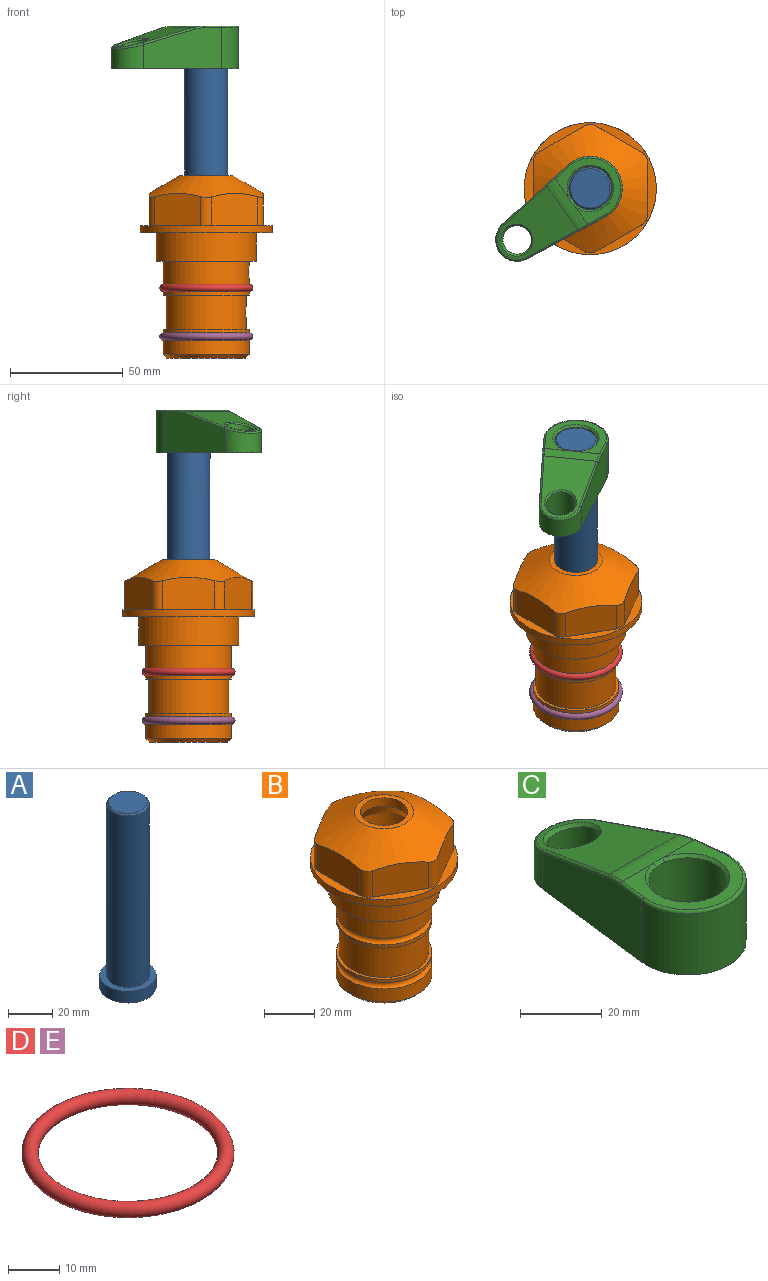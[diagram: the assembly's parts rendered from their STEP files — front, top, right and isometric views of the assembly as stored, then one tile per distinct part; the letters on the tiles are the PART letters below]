
ASSEMBLY  parts=5 mates=4
PART A: 6 faces, bbox 25.4x25.4x101.6 mm
  f0: plane 17.46x17.46mm, normal (0,0,1), area 239.5mm2, adj f5
  f1: plane 25.4x25.4mm, normal (0,0,-1), area 506.7mm2, adj f2
  f2: cylinder r=12.7mm len=25.4mm, axis (0,0,1), area 506.7mm2, adj f1,f3
  f3: plane 25.4x25.4mm, normal (0,0,1), area 221.7mm2, adj f2,f4
  f4: cylinder r=9.53mm len=94.46mm, axis (0,0,1), area 5653mm2, adj f3,f5
  f5: cone r=8.73mm half-angle=45deg, axis (0,0,-1), area 64.4mm2, adj f0,f4
PART B: 36 faces, bbox 58.7x58.7x81 mm
  f0: cylinder r=17.78mm len=35.56mm, axis (0,0,1), area 1670.8mm2, adj f23,f24,f31
  f1: cylinder r=19.05mm len=38.1mm, axis (0,0,1), area 1191.9mm2, adj f26,f27,f30
  f2: plane 58.66x58.66mm, normal (0,0,-1), area 1150.6mm2, adj f3,f28
  f3: cylinder r=29.33mm len=58.66mm, axis (0,0,-1), area 585.1mm2, adj f2,f4
  f4: plane 58.66x58.66mm, normal (0,0,1), area 475.9mm2, adj f3,f5,f6,f7,f8,f9,f10,f11
  f5: plane 20.32x14.34mm, normal (-0.5,0.87,0), area 324.4mm2, adj f4,f15,f16,f17
  f6: plane 20.32x14.34mm, normal (0.5,0.87,0), area 324.4mm2, adj f4,f14,f15,f17
  f7: plane 23.48x14.34mm, normal (1,0,0), area 324.4mm2, adj f4,f13,f14,f17
  f8: plane 20.32x14.34mm, normal (0.5,-0.87,0), area 324.4mm2, adj f4,f12,f13,f17
  f9: plane 20.32x14.34mm, normal (-0.5,-0.87,0), area 324.4mm2, adj f4,f11,f12,f17
  f10: plane 23.48x14.34mm, normal (-1,0,0), area 324.4mm2, adj f4,f11,f16,f17
  f11: cylinder r=5.08mm len=12.85mm, axis (0,0,-1), area 67.2mm2, adj f4,f9,f10,f17
  f12: cylinder r=5.08mm len=12.85mm, axis (0,0,-1), area 67.2mm2, adj f4,f8,f9,f17
  f13: cylinder r=5.08mm len=12.85mm, axis (0,0,-1), area 67.2mm2, adj f4,f7,f8,f17
  f14: cylinder r=5.08mm len=12.85mm, axis (0,0,-1), area 67.2mm2, adj f4,f6,f7,f17
  f15: cylinder r=5.08mm len=12.85mm, axis (0,0,-1), area 67.2mm2, adj f4,f5,f6,f17
  f16: cylinder r=5.08mm len=12.85mm, axis (0,0,-1), area 67.2mm2, adj f4,f5,f10,f17
  f17: cone r=11.73mm half-angle=60deg, axis (0,0,-1), area 2071.8mm2, adj f5,f6,f7,f8,f9,f10,f11,f12
  f18: plane 23.46x23.46mm, normal (0,0,1), area 147.4mm2, adj f17,f35
  f19: plane 34.93x34.93mm, normal (0,0,-1), area 958mm2, adj f29
  f20: cylinder r=19.05mm len=38.1mm, axis (0,0,1), area 760.1mm2, adj f21,f29
  f21: torus R=19.05mm, axis (0,0,1), area 565.3mm2, adj f20,f22
  f22: cylinder r=19.05mm len=38.1mm, axis (0,0,1), area 190mm2, adj f21,f23
  f23: plane 38.1x38.1mm, normal (0,0,1), area 146.9mm2, adj f0,f22
  f24: plane 38.1x38.1mm, normal (0,0,-1), area 146.9mm2, adj f0,f25
  f25: cylinder r=19.05mm len=38.1mm, axis (0,0,1), area 190mm2, adj f24,f26
  f26: torus R=19.05mm, axis (0,0,1), area 565.3mm2, adj f1,f25
  f27: plane 44.45x44.45mm, normal (0,0,-1), area 411.7mm2, adj f1,f28
  f28: cylinder r=22.23mm len=44.45mm, axis (0,0,1), area 1773.5mm2, adj f2,f27
  f29: cone r=19.05mm half-angle=45deg, axis (0,0,1), area 257.5mm2, adj f19,f20
  f30: cylinder r=3.17mm len=6.75mm, axis (-1,0,0), area 128mm2, adj f1,f33
  f31: cylinder r=3.17mm len=6.35mm, axis (-1,0,0), area 102.5mm2, adj f0,f33
  f32: plane 25.4x25.4mm, normal (0,0,1), area 506.7mm2, adj f33
  f33: cylinder r=12.7mm len=66.42mm, axis (0,0,-1), area 5236.2mm2, adj f30,f31,f32,f34
  f34: cone r=9.53mm half-angle=30deg, axis (0,0,-1), area 443.4mm2, adj f33,f35
  f35: cylinder r=9.53mm len=19.05mm, axis (0,0,-1), area 240.9mm2, adj f18,f34
PART C: 31 faces, bbox 31.7x65.5x19.8 mm
  f0: plane 39.12x18.26mm, normal (0.99,0.12,0), area 612.2mm2, adj f1,f4,f7,f11,f13,f15
  f1: cylinder r=9.53mm len=18.91mm, axis (0,0,-1), area 296.1mm2, adj f0,f2,f7,f17
  f2: plane 39.12x18.26mm, normal (-0.99,0.12,0), area 612.2mm2, adj f1,f4,f7,f12,f14,f16
  f3: cylinder r=6.35mm len=12.7mm, axis (0,0,-1), area 362.4mm2, adj f7,f18
  f4: cylinder r=14.29mm len=28.58mm, axis (0,0,-1), area 882.2mm2, adj f0,f2,f7,f10
  f5: cylinder r=9.53mm len=19.05mm, axis (0,0,-1), area 1092.6mm2, adj f7,f19,f20
  f6: plane 26.99x23.69mm, normal (0,0,1), area 216.2mm2, adj f9,f10,f11,f12,f19
  f7: plane 63.5x28.58mm, normal (0,0,-1), area 661.8mm2, adj f0,f1,f2,f3,f4,f5,f22,f23
  f8: plane 33.52x23.6mm, normal (0,0.26,0.97), area 486mm2, adj f9,f15,f16,f17,f18
  f9: cylinder r=19.05mm len=24.72mm, axis (1,0,0), area 120.4mm2, adj f6,f8,f13,f14,f20
  f10: torus R=13.49mm, axis (0,0,1), area 59mm2, adj f4,f6,f11,f12
  f11: cylinder r=0.79mm len=8.67mm, axis (0.12,-0.99,0), area 10.8mm2, adj f0,f6,f10,f13
  f12: cylinder r=0.79mm len=8.67mm, axis (0.12,0.99,0), area 10.8mm2, adj f2,f6,f10,f14
  f13: bspline ~4.95x1.42mm, area 6.1mm2, adj f0,f9,f11,f15
  f14: bspline ~4.95x1.42mm, area 6.1mm2, adj f2,f9,f12,f16
  f15: cylinder r=0.79mm len=25.95mm, axis (0.12,-0.96,0.26), area 32.9mm2, adj f0,f8,f13,f17
  f16: cylinder r=0.79mm len=25.95mm, axis (0.12,0.96,-0.26), area 32.9mm2, adj f2,f8,f14,f17
  f17: bspline ~18.91x8.38mm, area 30mm2, adj f1,f8,f15,f16
  f18: bspline ~14.29x14.29mm, area 48.3mm2, adj f3,f8
  f19: cone r=9.53mm half-angle=45deg, axis (0,0,1), area 66.5mm2, adj f5,f6,f20
  f20: bspline ~3.22x0.96mm, area 3.5mm2, adj f5,f9,f19
  f21: plane 2.75x2.72mm, normal (0,0,-1), area 2.9mm2, adj f23,f25,f28
  f22: plane 23.05x15.88mm, normal (-0.99,-0.12,0), area 323.6mm2, adj f7,f25,f26,f27,f28,f29
  f23: plane 23.05x15.88mm, normal (0.99,-0.12,0), area 323.6mm2, adj f7,f21,f25,f27,f28,f30
  f24: cylinder r=9.53mm len=10.69mm, axis (0,0,-1), area 114.7mm2, adj f7,f27,f29,f30
  f25: cylinder r=12.7mm len=20.59mm, axis (0,0,-1), area 381.1mm2, adj f7,f21,f22,f23,f26,f28
  f26: plane 2.75x2.72mm, normal (0,0,-1), area 2.9mm2, adj f22,f25,f28
  f27: plane 19.72x18.37mm, normal (0,-0.26,-0.97), area 291.8mm2, adj f22,f23,f24,f28,f29,f30
  f28: cylinder r=15.88mm len=19.92mm, axis (1,0,0), area 54.8mm2, adj f21,f22,f23,f25,f26,f27
  f29: cylinder r=1.59mm len=11mm, axis (0,0,-1), area 34.7mm2, adj f7,f22,f24,f27
  f30: cylinder r=1.59mm len=11mm, axis (0,0,-1), area 34.7mm2, adj f7,f23,f24,f27
PART D: 1 faces, bbox 44.7x44.7x3.2 mm
  f0: torus R=19.05mm, axis (0,0,1), area 1193.9mm2
PART E: same geometry as D
PLACE A rot(axis=(0,0,1),125.2deg) t=(0,0,27.55)mm
PLACE B at identity fixed
PLACE C rot(axis=(0,0,1),125.2deg) t=(0,0,28.35)mm
PLACE D at identity
PLACE E t=(0,0,-21.59)mm
MATE cylindrical A.f2 <-> B.f0  axis (0,0,-1) through (0,0,-10.55)mm
MATE fastened D.f0 <-> B.f0  axis (0,0,1) through (0,0,-24.51)mm
MATE fastened E.f0 <-> B.f0  axis (0,0,1) through (0,0,-46.1)mm
MATE fastened C.f4 <-> A.f2  axis (0,0,1) through (0,0,91.05)mm
